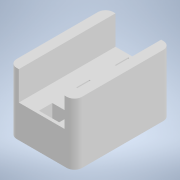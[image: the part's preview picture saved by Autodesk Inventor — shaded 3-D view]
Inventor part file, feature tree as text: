
AUTODESK INVENTOR PART (.ipt)
format: ipt  version: 2022 (Build 260153000, 153)  size: 188,928 bytes
history: native  units: mm
features: extrude x4, sketch x4, projected_geometry x2, other x1, fillet x1
ambient origin geometry x8: Origin, YZ Plane, XZ Plane, XY Plane, X Axis, Y Axis, Z Axis, Center Point
bodies: Body1 (feature_tree)
feature tree (12):
  other  "Твердое тело1"
  extrude  "Выдавливание1"  Depth=5.8mm
  extrude  "Выдавливание2"  Depth=12.85mm
  extrude  "Выдавливание3"  Depth=6.0mm
  extrude  "Выдавливание4"  Depth=12.7mm
  fillet  "Сопряжение1"  Radius=1.3mm
  sketch  "Эскиз1"
  sketch  "Эскиз2"
  sketch  "Эскиз3"
  projected_geometry  "Спроецированная петля1"
  sketch  "Эскиз4"
  projected_geometry  "Спроецированная петля2"
